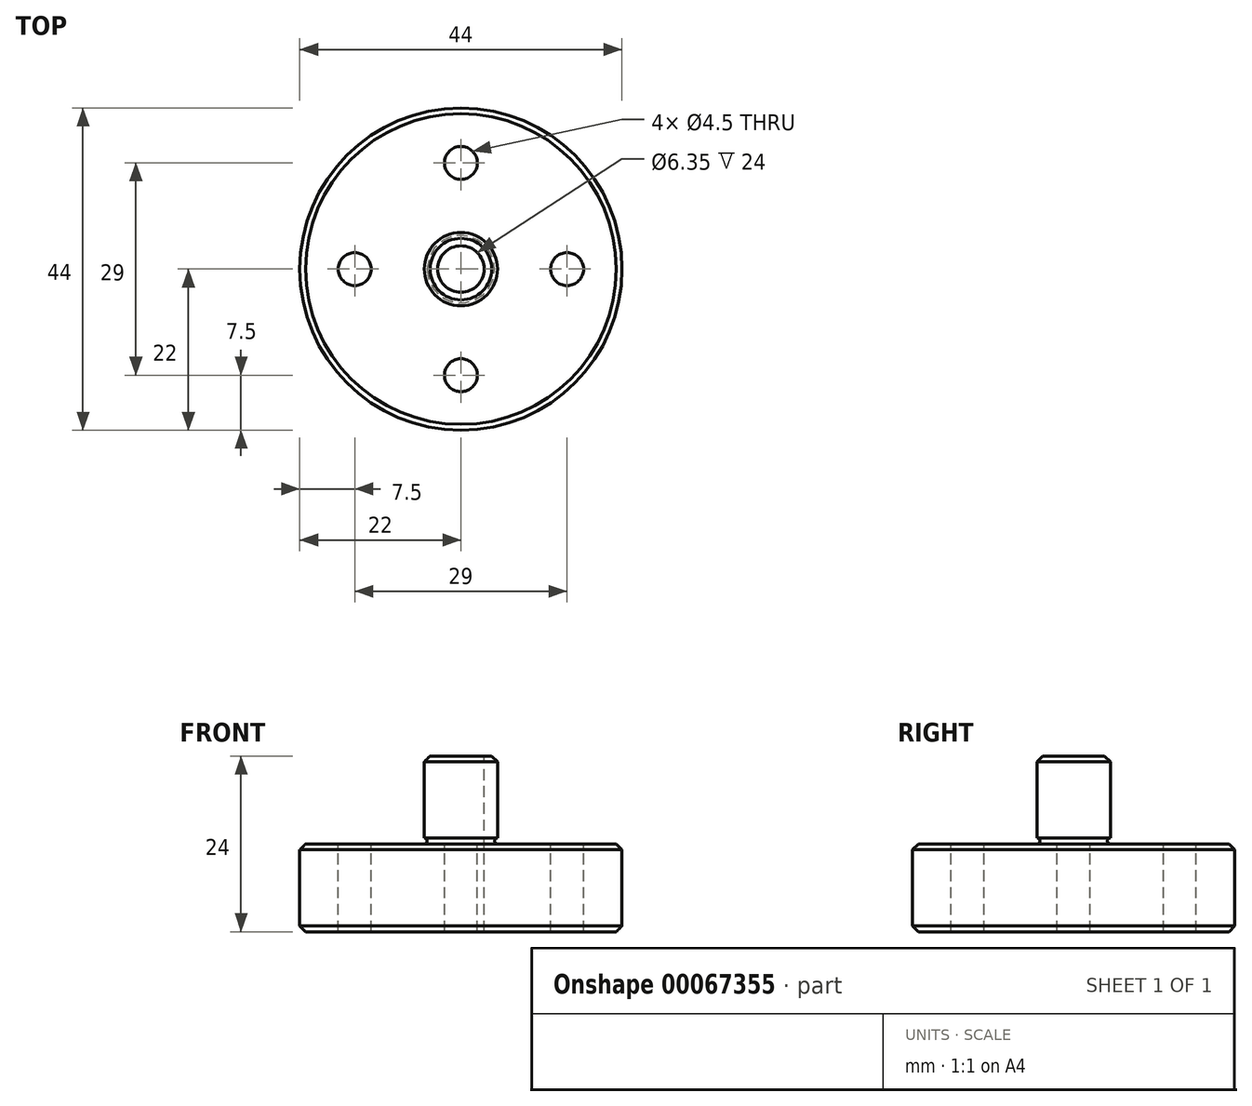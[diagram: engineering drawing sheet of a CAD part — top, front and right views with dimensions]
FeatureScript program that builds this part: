
annotation { "Feature Type Name" : "Feature", "Feature Type Description" : "" }
export const myFeature = defineFeature(function(context is Context, id is Id, definition is map)
    precondition{}
    {
        {
            var Q0;
            Q0=qCreatedBy(makeId("Front.planeOp"),FACE);
            var sketch = newSketch(context, id + "F0", { "sketchPlane" : qUnion([Q0])});
            skLineSegment(sketch, "E0", {"start": v(0, 0) * mm, "end": v(0, 24) * mm});
            skLineSegment(sketch, "E1", {"start": v(0, 24) * mm, "end": v(5, 24) * mm});
            skLineSegment(sketch, "E2", {"start": v(5, 24) * mm, "end": v(5, 12.8) * mm});
            skLineSegment(sketch, "E3", {"start": v(5, 12) * mm, "end": v(22, 12) * mm});
            skLineSegment(sketch, "E4", {"start": v(22, 12) * mm, "end": v(22, 0) * mm});
            skLineSegment(sketch, "E5", {"start": v(22, 0) * mm, "end": v(0, 0) * mm});
            skArc(sketch, "E6", {"start": v(5, 12) * mm, "mid": v(4.6, 12.4) * mm, "end": v(5, 12.8) * mm});
            skSolve(sketch);
        }
        {
            var Q0;
            Q0 = qSketchRegion(id + "F0", true);
            var Q1;
            Q1=sQuery(id+"F0.wireOp",EDGE,"E0");
            revolve(context, id + "F1", {"entities" : qUnion([Q0]), "axis" : qUnion([Q1]), "revolveType" : RevolveType.FULL});
        }
        {
            var Q0;
            Q0=makeQuery(id+"F1.opRevolve","SWEPT_FACE",FACE,{"disambiguationData":[OSD([sQuery(id+"F0.wireOp",EDGE,"E1")])]});
            var sketch = newSketch(context, id + "F2", { "sketchPlane" : qUnion([Q0])});
            skPoint(sketch, "E7", {"position": v(0, 0) * mm});
            skSolve(sketch);
        }
        {
            var Q0;
            Q0=sQuery(id+"F2.wireOp",VERTEX,"E7");
            var Q1;
            Q1=makeQuery(id+"F1.opRevolve","SWEPT_BODY",BODY,{"disambiguationData":[OSD([sQuery(id+"F0.wireOp",EDGE,"E0"),sQuery(id+"F0.wireOp",EDGE,"E1"),sQuery(id+"F0.wireOp",EDGE,"E2"),sQuery(id+"F0.wireOp",EDGE,"E3"),sQuery(id+"F0.wireOp",EDGE,"E4"),sQuery(id+"F0.wireOp",EDGE,"E5")])]});
            hole(context, id + "F3", {"style" : HoleStyle.SIMPLE, "holeDiameter" : 6.35 * mm, "endStyle" : HoleEndStyle.THROUGH, "locations" : qUnion([Q0]), "scope" : qUnion([Q1])});
        }
        {
            var Q0;
            Q0=makeQuery(id+"F1.opRevolve","SWEPT_FACE",FACE,{"disambiguationData":[OSD([sQuery(id+"F0.wireOp",EDGE,"E3")])]});
            var sketch = newSketch(context, id + "F4", { "sketchPlane" : qUnion([Q0])});
            skPoint(sketch, "E8", {"position": v(-14.5, 0) * mm});
            skCircle(sketch, "E9", {"center": v(0, 0) * mm, "radius": 14.5 * mm});
            skPoint(sketch, "E10", {"position": v(0, 14.5) * mm});
            skPoint(sketch, "E11", {"position": v(14.5, 0) * mm});
            skPoint(sketch, "E12", {"position": v(0, -14.5) * mm});
            skSolve(sketch);
        }
        {
            var Q0;
            Q0=sQuery(id+"F4.wireOp",VERTEX,"E10");
            var Q1;
            Q1=sQuery(id+"F4.wireOp",VERTEX,"E8");
            var Q2;
            Q2=sQuery(id+"F4.wireOp",VERTEX,"E12");
            var Q3;
            Q3=sQuery(id+"F4.wireOp",VERTEX,"E11");
            var Q4;
            Q4=makeQuery(id+"F1.opRevolve","SWEPT_BODY",BODY,{"disambiguationData":[OSD([sQuery(id+"F0.wireOp",EDGE,"E0"),sQuery(id+"F0.wireOp",EDGE,"E1"),sQuery(id+"F0.wireOp",EDGE,"E2"),sQuery(id+"F0.wireOp",EDGE,"E3"),sQuery(id+"F0.wireOp",EDGE,"E4"),sQuery(id+"F0.wireOp",EDGE,"E5")])]});
            hole(context, id + "F5", {"style" : HoleStyle.SIMPLE, "holeDiameter" : 4.5 * mm, "endStyle" : HoleEndStyle.THROUGH, "locations" : qUnion([Q0, Q1, Q2, Q3]), "scope" : qUnion([Q4])});
        }
        {
            var Q0;
            Q0=makeQuery(id+"F1.opRevolve","SWEPT_EDGE",EDGE,{"disambiguationData":[OSD([sQuery(id+"F0.wireOp",EDGE,"E3"),sQuery(id+"F0.wireOp",EDGE,"E4")])]});
            var Q1;
            Q1=makeQuery(id+"F1.opRevolve","SWEPT_FACE",FACE,{"disambiguationData":[OSD([sQuery(id+"F0.wireOp",EDGE,"E4")])]});
            var Q2;
            Q2=makeQuery(id+"F1.opRevolve","SWEPT_EDGE",EDGE,{"disambiguationData":[OSD([sQuery(id+"F0.wireOp",EDGE,"E1"),sQuery(id+"F0.wireOp",EDGE,"E2")])]});
            chamfer(context, id + "F6", {"entities" : qUnion([Q0, Q1, Q2]), "width" : 0.8 * mm, "tangentPropagation" : true});
        }
    });
